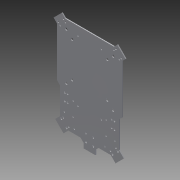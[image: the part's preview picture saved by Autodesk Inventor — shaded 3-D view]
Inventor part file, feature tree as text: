
AUTODESK INVENTOR PART (.ipt)
format: ipt  version: 2013 (Build 170138000, 138)  size: 6,251,520 bytes
history: native  units: mm
features: sketch x9, hole x5, extrude x4, other x2
ambient origin geometry x8: Origin, YZ Plane, XZ Plane, XY Plane, X Axis, Y Axis, Z Axis, Center Point
feature tree (20):
  other  "ソリッド1"
  extrude  "押し出し1"  Depth=115.0mm
  hole  "穴1"  [1 undecoded]
  hole  "穴2"  [1 undecoded]
  hole  "穴6"  [1 undecoded]
  hole  "穴7"  [1 undecoded]
  hole  "穴8"  [1 undecoded]
  extrude  "押し出し5"  TaperAngle=0.0deg  [1 undecoded]
  extrude  "押し出し7"  Depth=2.0mm TaperAngle=0.0deg
  extrude  "押し出し8"  Depth=3.2mm
  sketch  "スケッチ1"
  sketch  "スケッチ2"
  sketch  "スケッチ3"
  sketch  "スケッチ9"
  sketch  "スケッチ11"
  sketch  "スケッチ12"
  sketch  "スケッチ13"
  sketch  "スケッチ14"
  sketch  "スケッチ17"
  other  "断面エッジを投影1"
note: 6 required parameter values undecoded (feature->parameter linkage not recoverable at this tier; creation-order binding heuristic only, values carry confidence <= 0.55)
